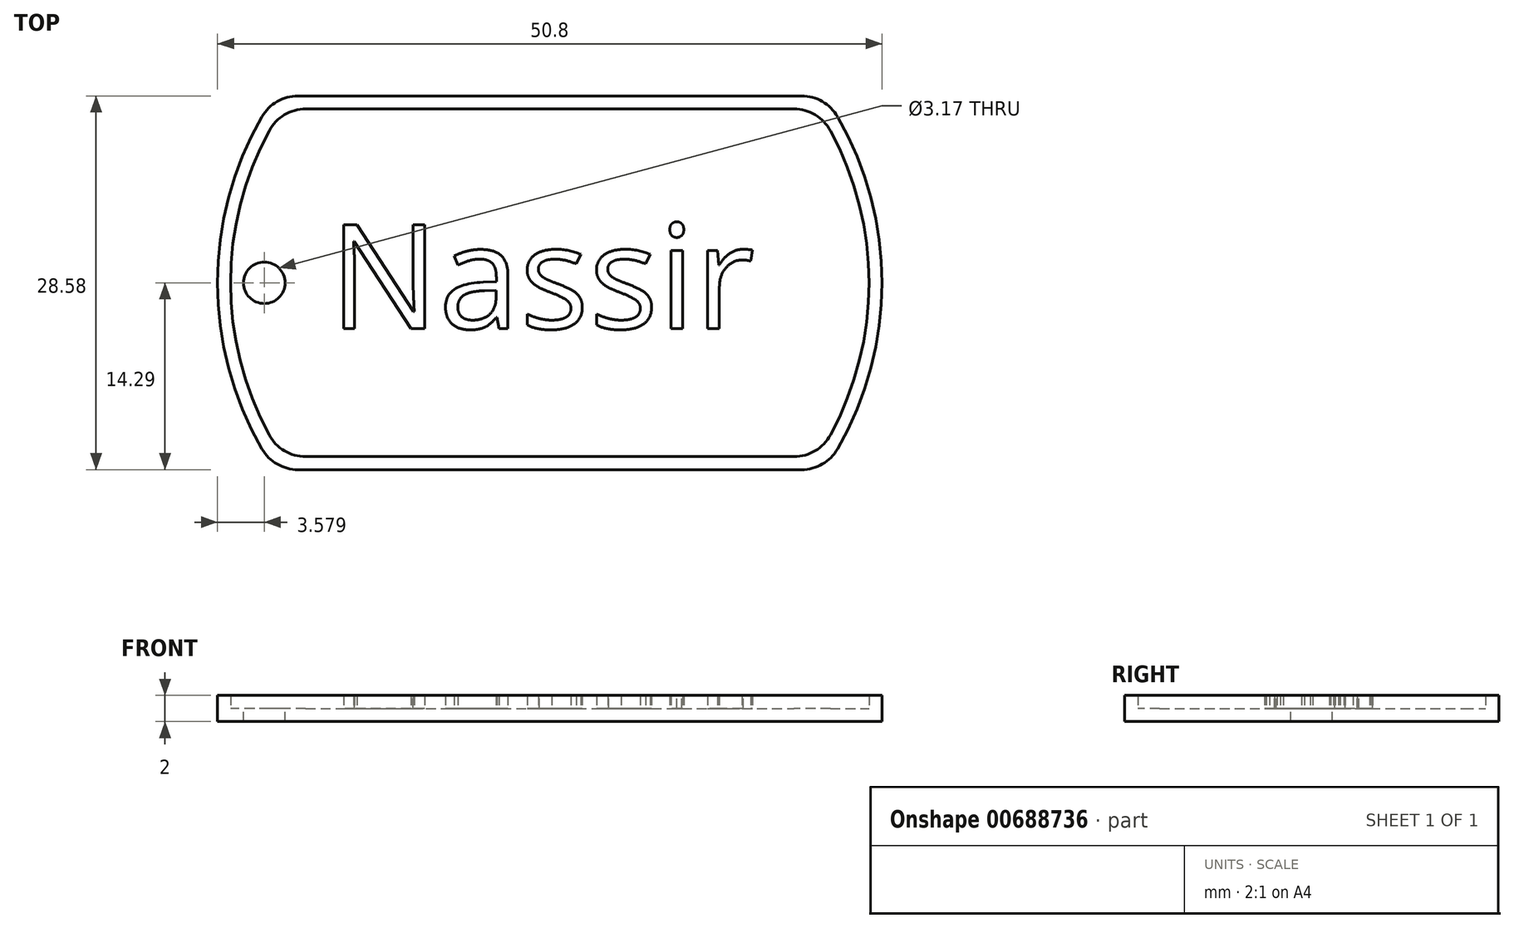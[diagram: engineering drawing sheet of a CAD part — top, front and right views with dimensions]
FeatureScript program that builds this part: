
annotation { "Feature Type Name" : "Feature", "Feature Type Description" : "" }
export const myFeature = defineFeature(function(context is Context, id is Id, definition is map)
    precondition{}
    {
        {
            var Q0;
            Q0=qCreatedBy(makeId("Top.planeOp"),FACE);
            var sketch = newSketch(context, id + "F0", { "sketchPlane" : qUnion([Q0])});
            skArc(sketch, "E0", {"start": v(-22, 12.7) * mm, "mid": v(-25.4, 0) * mm, "end": v(-22, -12.7) * mm});
            skLineSegment(sketch, "E1.top", {"start": v(-19.25, -14.29) * mm, "end": v(19.25, -14.29) * mm});
            skArc(sketch, "E2.trimOffspring", {"start": v(22, -12.7) * mm, "mid": v(25.4, 0) * mm, "end": v(22, 12.7) * mm});
            skLineSegment(sketch, "E3", {"start": v(-19.25, 14.29) * mm, "end": v(19.25, 14.29) * mm});
            skPoint(sketch, "E4.visualSharp", {"position": v(-21, 14.29) * mm});
            skArc(sketch, "E4.filletArc", {"start": v(-19.25, 14.29) * mm, "mid": v(-20.83, 13.86) * mm, "end": v(-22, 12.7) * mm});
            skPoint(sketch, "E5.visualSharp", {"position": v(21, 14.29) * mm});
            skArc(sketch, "E5.filletArc", {"start": v(22, 12.7) * mm, "mid": v(20.83, 13.86) * mm, "end": v(19.25, 14.29) * mm});
            skPoint(sketch, "E6.visualSharp", {"position": v(21, -14.29) * mm});
            skArc(sketch, "E6.filletArc", {"start": v(19.25, -14.29) * mm, "mid": v(20.83, -13.86) * mm, "end": v(22, -12.7) * mm});
            skPoint(sketch, "E7.visualSharp", {"position": v(-21, -14.29) * mm});
            skArc(sketch, "E7.filletArc", {"start": v(-22, -12.7) * mm, "mid": v(-20.83, -13.86) * mm, "end": v(-19.25, -14.29) * mm});
            skSolve(sketch);
        }
        {
            var Q0;
            Q0=makeQuery(id+"F0.imprint","IMPRINT",FACE,{"disambiguationData":[TD([[makeQuery(id+"F0.imprint","IMPRINT",EDGE,{"derivedFrom":sQuery(id+"F0.wireOp",EDGE,"E0")}),1.0]])]});
            extrude(context, id + "F1", {"entities" : qUnion([Q0]), "depth" : 1 * mm, "offsetDistance" : 25.4 * mm});
        }
        {
            var Q0;
            Q0=makeQuery(id+"F1.opExtrude","CAP_FACE",FACE,{"disambiguationData":[OSD([sQuery(id+"F0.wireOp",EDGE,"E0"),sQuery(id+"F0.wireOp",EDGE,"E1.top"),sQuery(id+"F0.wireOp",EDGE,"E2.trimOffspring"),sQuery(id+"F0.wireOp",EDGE,"E3"),sQuery(id+"F0.wireOp",EDGE,"E4.filletArc"),sQuery(id+"F0.wireOp",EDGE,"E5.filletArc"),sQuery(id+"F0.wireOp",EDGE,"E6.filletArc"),sQuery(id+"F0.wireOp",EDGE,"E7.filletArc")])],"isStart":false});
            var sketch = newSketch(context, id + "F2", { "sketchPlane" : qUnion([Q0])});
            skLineSegment(sketch, "E8.0", {"start": v(-18.66, 13.29) * mm, "end": v(18.66, 13.29) * mm});
            skArc(sketch, "E8.1", {"start": v(-21.45, 11.63) * mm, "mid": v(-24.4, 0) * mm, "end": v(-21.45, -11.63) * mm});
            skLineSegment(sketch, "E8.2", {"start": v(-18.66, -13.29) * mm, "end": v(18.66, -13.29) * mm});
            skArc(sketch, "E8.3", {"start": v(21.45, -11.63) * mm, "mid": v(24.4, 0) * mm, "end": v(21.45, 11.63) * mm});
            skPoint(sketch, "E9.visualSharp", {"position": v(-20.46, 13.29) * mm});
            skArc(sketch, "E9.filletArc", {"start": v(-18.66, 13.29) * mm, "mid": v(-20.29, 12.84) * mm, "end": v(-21.45, 11.63) * mm});
            skPoint(sketch, "E10.visualSharp", {"position": v(20.46, 13.29) * mm});
            skArc(sketch, "E10.filletArc", {"start": v(21.45, 11.63) * mm, "mid": v(20.29, 12.84) * mm, "end": v(18.66, 13.29) * mm});
            skPoint(sketch, "E11.visualSharp", {"position": v(20.46, -13.29) * mm});
            skArc(sketch, "E11.filletArc", {"start": v(18.66, -13.29) * mm, "mid": v(20.29, -12.84) * mm, "end": v(21.45, -11.63) * mm});
            skPoint(sketch, "E12.visualSharp", {"position": v(-20.46, -13.29) * mm});
            skArc(sketch, "E12.filletArc", {"start": v(-21.45, -11.63) * mm, "mid": v(-20.29, -12.84) * mm, "end": v(-18.66, -13.29) * mm});
            skLineSegment(sketch, "E13.0", {"start": v(-19.25, 14.29) * mm, "end": v(19.25, 14.29) * mm});
            skArc(sketch, "E13.1", {"start": v(-22, 12.7) * mm, "mid": v(-25.4, 0) * mm, "end": v(-22, -12.7) * mm});
            skLineSegment(sketch, "E13.2", {"start": v(-19.25, -14.29) * mm, "end": v(19.25, -14.29) * mm});
            skArc(sketch, "E13.3", {"start": v(22, -12.7) * mm, "mid": v(25.4, 0) * mm, "end": v(22, 12.7) * mm});
            skPoint(sketch, "E14.visualSharp", {"position": v(-21, -14.29) * mm});
            skArc(sketch, "E14.filletArc", {"start": v(-22, -12.7) * mm, "mid": v(-20.83, -13.86) * mm, "end": v(-19.25, -14.29) * mm});
            skPoint(sketch, "E15.visualSharp", {"position": v(21, -14.29) * mm});
            skArc(sketch, "E15.filletArc", {"start": v(19.25, -14.29) * mm, "mid": v(20.83, -13.86) * mm, "end": v(22, -12.7) * mm});
            skPoint(sketch, "E16.visualSharp", {"position": v(21, 14.29) * mm});
            skArc(sketch, "E16.filletArc", {"start": v(22, 12.7) * mm, "mid": v(20.83, 13.86) * mm, "end": v(19.25, 14.29) * mm});
            skPoint(sketch, "E17.visualSharp", {"position": v(-21, 14.29) * mm});
            skArc(sketch, "E17.filletArc", {"start": v(-19.25, 14.29) * mm, "mid": v(-20.83, 13.86) * mm, "end": v(-22, 12.7) * mm});
            skSolve(sketch);
        }
        {
            var Q0;
            Q0=makeQuery(id+"F2.imprint","IMPRINT",FACE,{"disambiguationData":[TD([[makeQuery(id+"F2.imprint","IMPRINT",EDGE,{"derivedFrom":sQuery(id+"F2.wireOp",EDGE,"E8.0")}),1.0]])]});
            extrude(context, id + "F3", {"entities" : qUnion([Q0]), "operationType" : NewBodyOperationType.ADD, "depth" : 1 * mm, "offsetDistance" : 25.4 * mm});
        }
        {
            var Q0;
            Q0=makeQuery(id+"F1.opExtrude","CAP_FACE",FACE,{"disambiguationData":[OSD([sQuery(id+"F0.wireOp",EDGE,"E0"),sQuery(id+"F0.wireOp",EDGE,"E1.top"),sQuery(id+"F0.wireOp",EDGE,"E2.trimOffspring"),sQuery(id+"F0.wireOp",EDGE,"E3"),sQuery(id+"F0.wireOp",EDGE,"E4.filletArc"),sQuery(id+"F0.wireOp",EDGE,"E5.filletArc"),sQuery(id+"F0.wireOp",EDGE,"E6.filletArc"),sQuery(id+"F0.wireOp",EDGE,"E7.filletArc")])],"isStart":false});
            var sketch = newSketch(context, id + "F4", { "sketchPlane" : qUnion([Q0])});
            skCircle(sketch, "E18", {"center": v(-21.82, 0) * mm, "radius": 1.59 * mm});
            skSolve(sketch);
        }
        {
            var Q0;
            Q0=makeQuery(id+"F4.imprint","IMPRINT",FACE,{"disambiguationData":[TD([[makeQuery(id+"F4.imprint","IMPRINT",EDGE,{"derivedFrom":sQuery(id+"F4.wireOp",EDGE,"E18")}),1.0]])]});
            extrude(context, id + "F5", {"entities" : qUnion([Q0]), "operationType" : NewBodyOperationType.REMOVE, "oppositeDirection" : true, "depth" : 1 * mm, "offsetDistance" : 25.4 * mm});
        }
        {
            var Q0;
            Q0=makeQuery(id+"F1.opExtrude","CAP_FACE",FACE,{"disambiguationData":[OSD([sQuery(id+"F0.wireOp",EDGE,"E0"),sQuery(id+"F0.wireOp",EDGE,"E1.top"),sQuery(id+"F0.wireOp",EDGE,"E2.trimOffspring"),sQuery(id+"F0.wireOp",EDGE,"E3"),sQuery(id+"F0.wireOp",EDGE,"E4.filletArc"),sQuery(id+"F0.wireOp",EDGE,"E5.filletArc"),sQuery(id+"F0.wireOp",EDGE,"E6.filletArc"),sQuery(id+"F0.wireOp",EDGE,"E7.filletArc")])],"isStart":false});
            var sketch = newSketch(context, id + "F6", { "sketchPlane" : qUnion([Q0])});
            skText(sketch, "E19", { "text": "Nassir", "fontName": "OpenSans-Regular.ttf"});
            const initialGuessF6  = {"E19": [-0.01686, -0.00349, 1, 0, 0.008]};
            skSetInitialGuess(sketch, initialGuessF6);
            skSolve(sketch);
        }
        {
            var Q0;
            Q0 = qSketchRegion(id + "F6", true);
            extrude(context, id + "F7", {"entities" : qUnion([Q0]), "operationType" : NewBodyOperationType.ADD, "depth" : 1 * mm, "offsetDistance" : 25.4 * mm});
        }
    });
